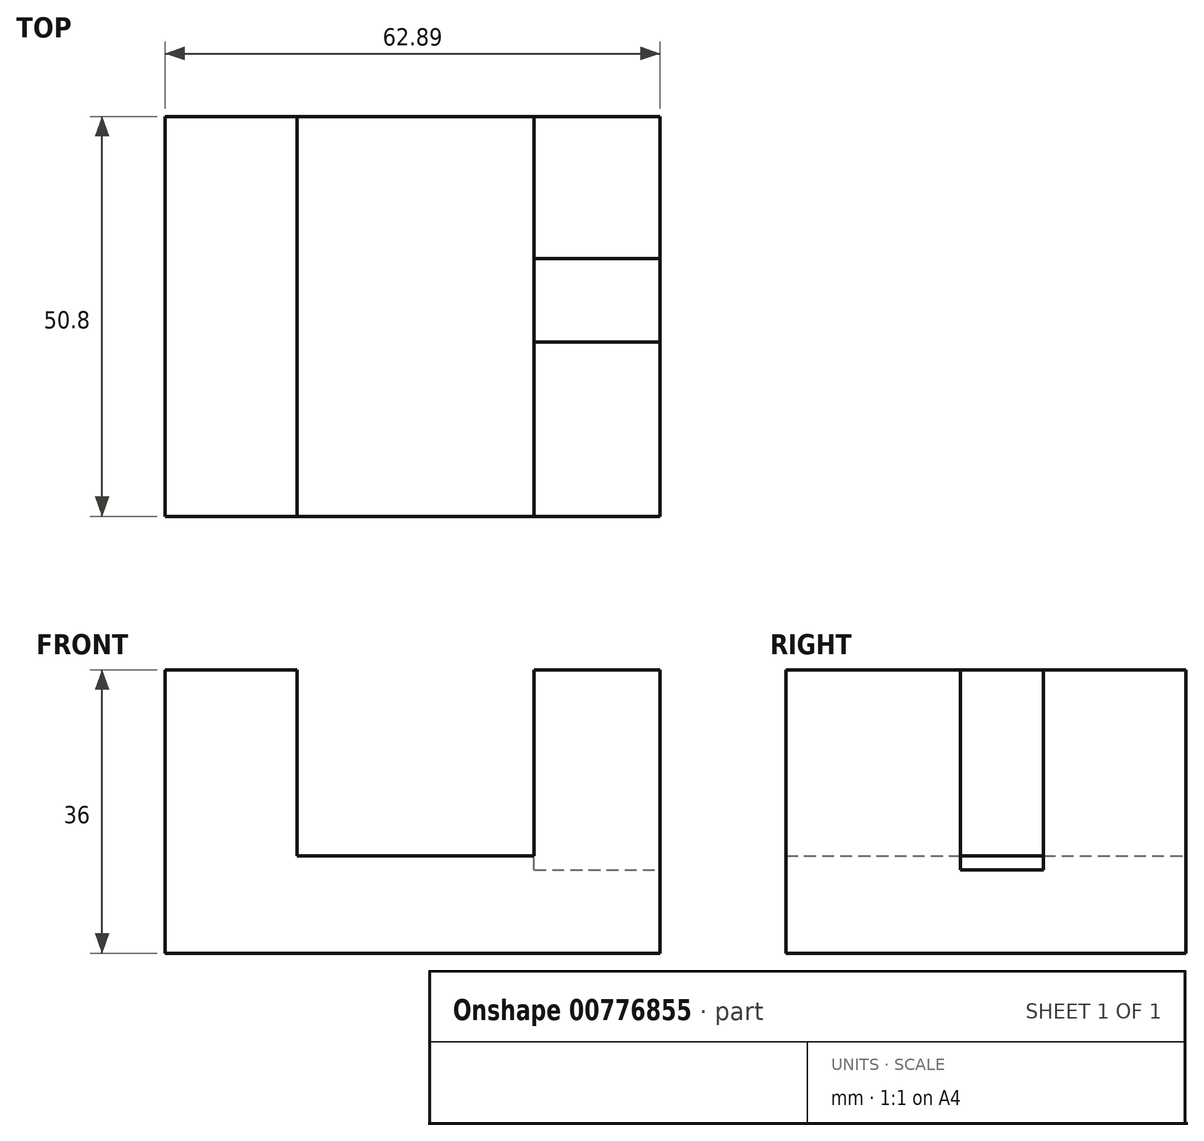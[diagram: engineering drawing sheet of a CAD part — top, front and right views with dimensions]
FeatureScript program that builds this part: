
annotation { "Feature Type Name" : "Feature", "Feature Type Description" : "" }
export const myFeature = defineFeature(function(context is Context, id is Id, definition is map)
    precondition{}
    {
        {
            var Q0;
            Q0=qCreatedBy(makeId("Front.planeOp"),FACE);
            var sketch = newSketch(context, id + "F0", { "sketchPlane" : qUnion([Q0])});
            skLineSegment(sketch, "E0.bottom", {"start": v(0, 0) * mm, "end": v(62.89, 0) * mm});
            skLineSegment(sketch, "E0.top", {"start": v(0, 36) * mm, "end": v(16.8, 36) * mm});
            skLineSegment(sketch, "E0.left", {"start": v(0, 0) * mm, "end": v(0, 36) * mm});
            skLineSegment(sketch, "E0.right", {"start": v(62.89, 0) * mm, "end": v(62.89, 36) * mm});
            skLineSegment(sketch, "E1.top", {"start": v(16.8, 12.33) * mm, "end": v(46.9, 12.33) * mm});
            skLineSegment(sketch, "E1.left", {"start": v(16.8, 36) * mm, "end": v(16.8, 12.33) * mm});
            skLineSegment(sketch, "E1.right", {"start": v(46.9, 36) * mm, "end": v(46.9, 12.33) * mm});
            skLineSegment(sketch, "E2.trimOffspring", {"start": v(46.9, 36) * mm, "end": v(62.89, 36) * mm});
            skSolve(sketch);
        }
        {
            var Q0;
            Q0=makeQuery(id+"F0.imprint","IMPRINT",FACE,{"disambiguationData":[TD([[makeQuery(id+"F0.imprint","IMPRINT",EDGE,{"derivedFrom":sQuery(id+"F0.wireOp",EDGE,"E0.bottom")}),1.0]])]});
            extrude(context, id + "F1", {"entities" : qUnion([Q0]), "depth" : 25.4 * mm, "offsetDistance" : 25.4 * mm});
        }
        {
            var Q0;
            Q0=makeQuery(id+"F1.opExtrude","CAP_FACE",FACE,{"disambiguationData":[OSD([sQuery(id+"F0.wireOp",EDGE,"E0.bottom"),sQuery(id+"F0.wireOp",EDGE,"E0.top"),sQuery(id+"F0.wireOp",EDGE,"E0.left"),sQuery(id+"F0.wireOp",EDGE,"E0.right"),sQuery(id+"F0.wireOp",EDGE,"E1.top"),sQuery(id+"F0.wireOp",EDGE,"E1.left"),sQuery(id+"F0.wireOp",EDGE,"E1.right"),sQuery(id+"F0.wireOp",EDGE,"E2.trimOffspring")])],"isStart":false});
            extrude(context, id + "F2", {"entities" : qUnion([Q0]), "operationType" : NewBodyOperationType.ADD, "depth" : 25.4 * mm, "offsetDistance" : 25.4 * mm});
        }
        {
            var Q0;
            {var subQ0=sQuery(id+"F0.wireOp",EDGE,"E2.trimOffspring");Q0=makeQuery(id+"F2.boolean.opBoolean","MERGE",FACE,{"derivedFrom":[makeQuery(id+"F1.opExtrude","SWEPT_FACE",FACE,{"disambiguationData":[OSD([subQ0])]}),makeQuery(id+"F2.opExtrude","SWEPT_FACE",FACE,{"disambiguationData":[OSD([subQ0])]})]});}
            var sketch = newSketch(context, id + "F3", { "sketchPlane" : qUnion([Q0])});
            skLineSegment(sketch, "E3.bottom", {"start": v(46.9, -18.08) * mm, "end": v(62.89, -18.08) * mm});
            skLineSegment(sketch, "E3.top", {"start": v(46.9, -28.64) * mm, "end": v(62.89, -28.64) * mm});
            skLineSegment(sketch, "E3.left", {"start": v(46.9, -18.08) * mm, "end": v(46.9, -28.64) * mm});
            skLineSegment(sketch, "E3.right", {"start": v(62.89, -18.08) * mm, "end": v(62.89, -28.64) * mm});
            skSolve(sketch);
        }
        {
            var Q0;
            Q0=makeQuery(id+"F3.imprint","IMPRINT",FACE,{"disambiguationData":[TD([[makeQuery(id+"F3.imprint","IMPRINT",EDGE,{"derivedFrom":sQuery(id+"F3.wireOp",EDGE,"E3.bottom")}),-1.0]])]});
            extrude(context, id + "F4", {"entities" : qUnion([Q0]), "operationType" : NewBodyOperationType.REMOVE, "oppositeDirection" : true, "depth" : 25.4 * mm, "offsetDistance" : 25.4 * mm});
        }
    });
